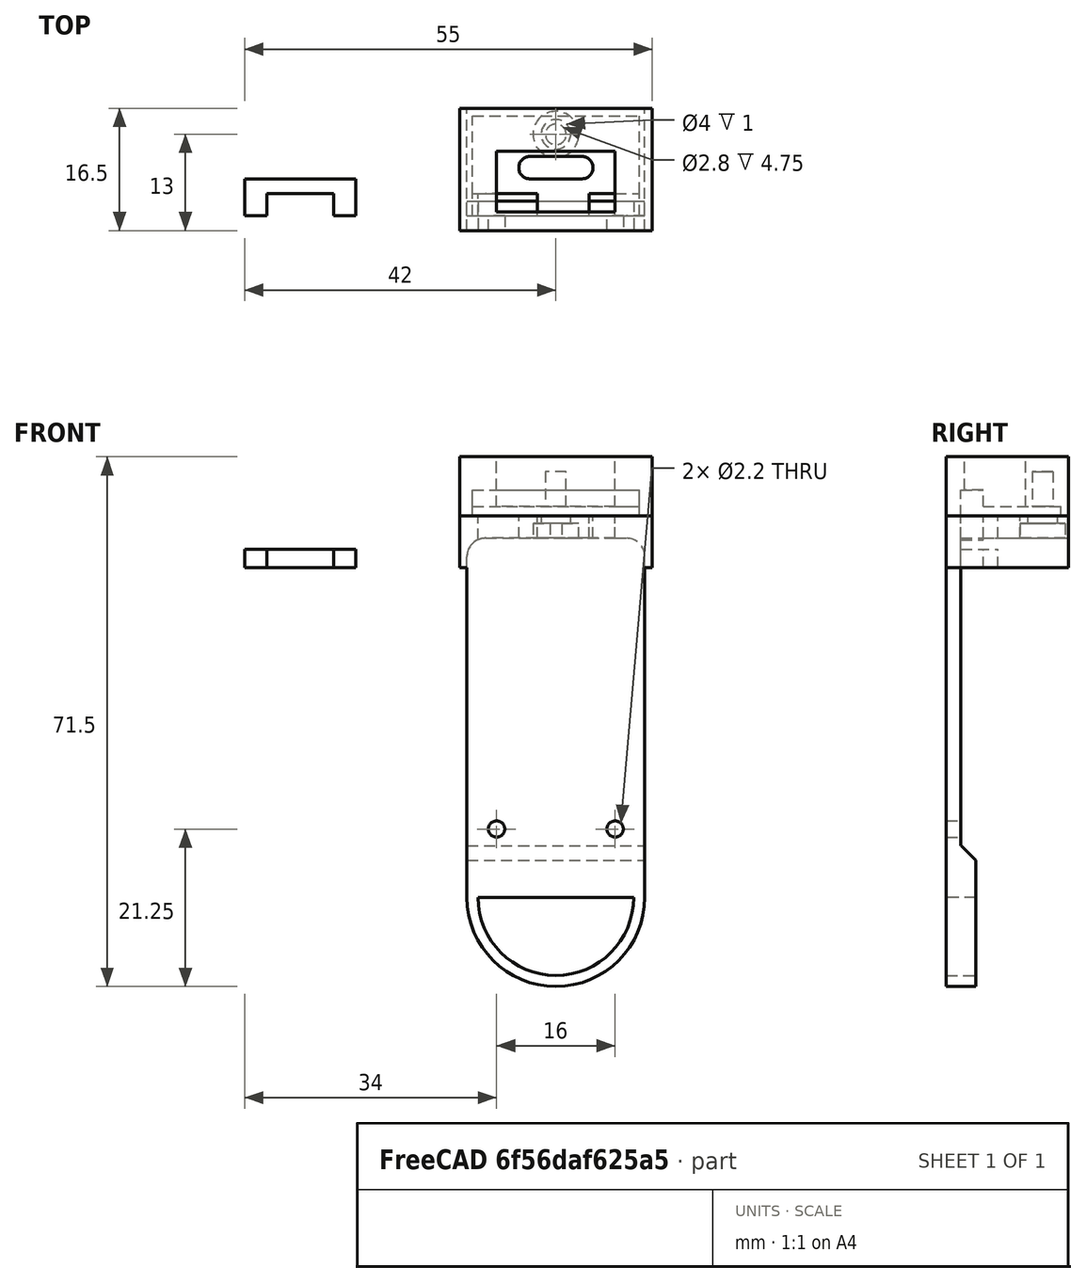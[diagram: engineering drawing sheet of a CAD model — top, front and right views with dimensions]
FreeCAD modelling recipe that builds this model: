
FCSTD DOCUMENT  (FreeCAD 1.0R39319 (Git))
Label: m5stick_dht22
License: All rights reserved
LicenseURL: http://en.wikipedia.org/wiki/All_rights_reserved
objects: Part::Box×13, Part::Cylinder×7, Part::Cut×6, Part::MultiFuse×5, Part::Fillet×2, Part::Chamfer×1
note: 34 computed .brp shape members not serialized (recipe doc carries the construction recipe); baked Part::Feature solids carry a one-line shape summary decoded from their .brp

FEATURE [Part::Box] Box  label="Cube(inner_base)"
  AttacherType = Attacher::AttachEngine3D
  Height = 4
  Length = 24
  Width = 14.5
FEATURE [Part::Box] Box001  label="Cube(outer_base)"
  AttacherType = Attacher::AttachEngine3D
  Height = 7
  Length = 26
  Placement = pos=(-1,-2,0) rot=(0,0,1;0rad)
  Width = 16.5
FEATURE [Part::Fillet] Fillet
  Base = -> Box
  EdgeLinks = -> Box [Edge2,Edge6]
  Edges = 2 edges r=2.5: [Edge2,Edge6]
FEATURE [Part::Box] Box002  label="Cube(header_cutter_big)"
  AttacherType = Attacher::AttachEngine3D
  Height = 7
  Length = 8
  Placement = pos=(1.5,0,0) rot=(0,0,1;0rad)
  Width = 3
FEATURE [Part::Box] Box003  label="Cube(ir_reciever_header_cutter)"
  AttacherType = Attacher::AttachEngine3D
  Height = 7
  Length = 10
  Placement = pos=(7,5,0) rot=(0,0,1;0rad)
  Width = 3
FEATURE [Part::Fillet] Fillet001
  Base = -> Box003
  EdgeLinks = -> Box003 [Edge1,Edge3,Edge5,Edge7]
  Edges = 4 edges r=1.45: [Edge1,Edge3,Edge5,Edge7]
FEATURE [Part::Box] Box004  label="Cube(pcb_cut)"
  AttacherType = Attacher::AttachEngine3D
  Height = 3.5
  Length = 22.5
  Placement = pos=(0.75,0,7) rot=(0,0,1;0rad)
  Width = 3
FEATURE [Part::Box] Box005  label="Cube(top_cover)"
  AttacherType = Attacher::AttachEngine3D
  Height = 8
  Length = 26
  Placement = pos=(-1,-2,7) rot=(0,0,1;0rad)
  Width = 16.5
FEATURE [Part::Box] Box007  label="Cube(back_cover)"
  AttacherType = Attacher::AttachEngine3D
  Height = 43.5
  Length = 24
  Placement = pos=(0,-2,-37.5) rot=(0,0,1;0rad)
  Width = 2
FEATURE [Part::Cylinder] Cylinder001  label="Cylinder001(right_bolt_clear)"
  Angle = 360
  AttacherType = Attacher::AttachEngine3D
  FirstAngle = 0
  Height = 10
  Placement = pos=(4,0,-35.25) rot=(1,0,0;1.5708rad)
  Radius = 1.1
  SecondAngle = 0
FEATURE [Part::Cylinder] Cylinder002  label="Cylinder002(left_bolt_clear)"
  Angle = 360
  AttacherType = Attacher::AttachEngine3D
  FirstAngle = 0
  Height = 10
  Placement = pos=(20,0,-35.25) rot=(1,0,0;1.5708rad)
  Radius = 1.1
  SecondAngle = 0
FEATURE [Part::MultiFuse] Fusion004
  Shapes = -> [Cylinder002,Cylinder001]
FEATURE [Part::Cylinder] Cylinder005  label="Cylinder005(bolt_head)"
  Angle = 360
  AttacherType = Attacher::AttachEngine3D
  FirstAngle = 0
  Height = 2
  Placement = pos=(12,11,4) rot=(0,0,1;0rad)
  Radius = 3.1
  SecondAngle = 0
FEATURE [Part::Cut] Cut
  Base = -> Box001
  Tool = -> Fillet
FEATURE [Part::Cylinder] Cylinder006  label="Cylinder005(bolt_clear)"
  Angle = 360
  AttacherType = Attacher::AttachEngine3D
  FirstAngle = 0
  Height = 2
  Placement = pos=(12,11,5) rot=(0,0,1;0rad)
  Radius = 2
  SecondAngle = 0
FEATURE [Part::Cylinder] Cylinder007  label="Cylinder005(bolt_thread)"
  Angle = 360
  AttacherType = Attacher::AttachEngine3D
  FirstAngle = 0
  Height = 6
  Placement = pos=(12,11,7) rot=(0,0,1;0rad)
  Radius = 1.4
  SecondAngle = 0
FEATURE [Part::Box] Box011  label="Cube(back_rest)"
  AttacherType = Attacher::AttachEngine3D
  Height = 7
  Length = 24
  Placement = pos=(0,-2,-44.5) rot=(0,0,1;0rad)
  Width = 4
FEATURE [Part::Cylinder] Cylinder008  label="Cylinder008(outer_hook)"
  Angle = 180
  AttacherType = Attacher::AttachEngine3D
  FirstAngle = 0
  Height = 4
  Placement = pos=(12,2,-44.5) rot=(0,0.707107,-0.707107;3.14159rad)
  Radius = 12
  SecondAngle = 0
FEATURE [Part::Cylinder] Cylinder009  label="Cylinder008(inner_hook)"
  Angle = 180
  AttacherType = Attacher::AttachEngine3D
  FirstAngle = 0
  Height = 4
  Placement = pos=(12,2,-44.5) rot=(0,0.707107,-0.707107;3.14159rad)
  Radius = 10.5
  SecondAngle = 0
FEATURE [Part::MultiFuse] Fusion008
  Shapes = -> [Box011,Cylinder008]
FEATURE [Part::Cut] Cut004
  Base = -> Fusion008
  Tool = -> Cylinder009
FEATURE [Part::Cut] Cut005
  Base = -> Box007
  Tool = -> Fusion004
FEATURE [Part::Box] Box012  label="Cube(pcb_cut)001"
  AttacherType = Attacher::AttachEngine3D
  Height = 1.25
  Length = 22.5
  Placement = pos=(0.75,3,7) rot=(0,0,1;0rad)
  Width = 10.5
FEATURE [Part::Box] Box013  label="Cube(dht22_support_outer)"
  AttacherType = Attacher::AttachEngine3D
  Height = 2.5
  Length = 15
  Placement = pos=(-30,0,0) rot=(0,0,1;0rad)
  Width = 5
FEATURE [Part::Box] Box014  label="Cube(dht22_support_inner)"
  AttacherType = Attacher::AttachEngine3D
  Height = 2.5
  Length = 9
  Placement = pos=(-27,0,0) rot=(0,0,1;0rad)
  Width = 3
FEATURE [Part::Cut] Cut007  label="Cut007(dht22_support)"
  Base = -> Box013
  Tool = -> Box014
FEATURE [Part::Box] Box015  label="Cube(header_cutter_small)"
  AttacherType = Attacher::AttachEngine3D
  Height = 7
  Length = 3.5
  Placement = pos=(16.5,0,0) rot=(0,0,1;0rad)
  Width = 3
FEATURE [Part::MultiFuse] Fusion
  Shapes = -> [Box015,Cylinder006,Cylinder005,Box002,Fillet001]
FEATURE [Part::Cut] Cut008
  Base = -> Cut
  Tool = -> Fusion
FEATURE [Part::MultiFuse] Fusion009
  Shapes = -> [Cut008,Cut005,Cut004]
FEATURE [Part::Chamfer] Chamfer  label="Chamfer(base)"
  Base = -> Fusion009
  EdgeLinks = -> Fusion009 [Edge141]
  Edges = 1 edges r=1.95: [Edge141]
FEATURE [Part::Box] Box017  label="Cube(dht22)"
  AttacherType = Attacher::AttachEngine3D
  Height = 10
  Length = 16
  Placement = pos=(4,0.5,7) rot=(0,0,1;0rad)
  Width = 8.25
FEATURE [Part::MultiFuse] Fusion010
  Shapes = -> [Cylinder007,Box012,Box017,Box004]
FEATURE [Part::Cut] Cut009  label="Cut009(cover)"
  Base = -> Box005
  Tool = -> Fusion010
